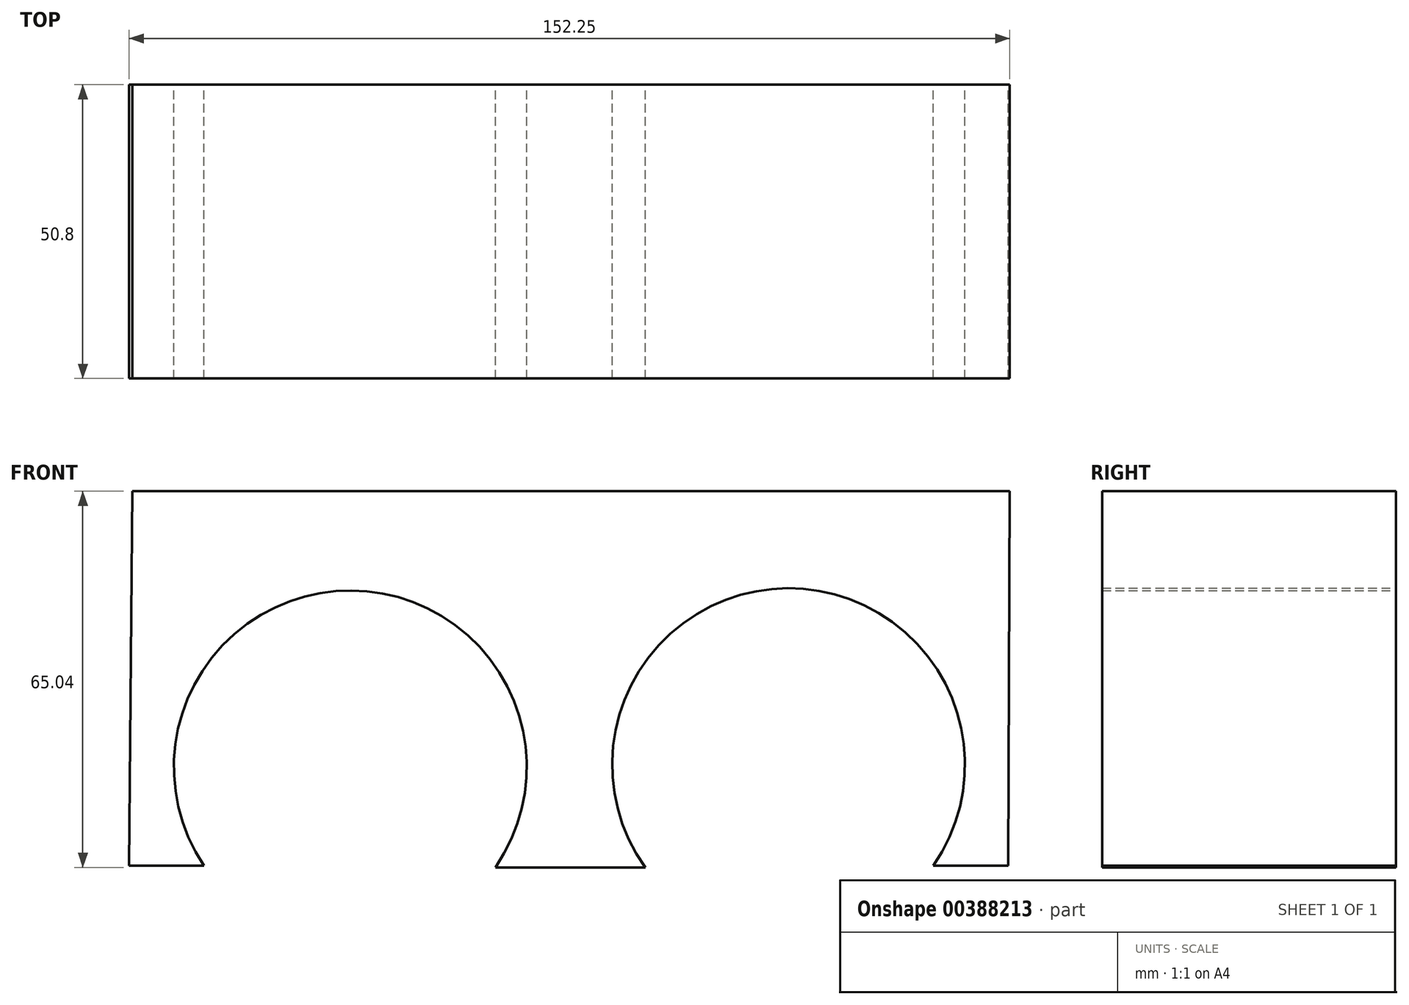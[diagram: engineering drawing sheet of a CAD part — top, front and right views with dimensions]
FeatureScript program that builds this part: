
annotation { "Feature Type Name" : "Feature", "Feature Type Description" : "" }
export const myFeature = defineFeature(function(context is Context, id is Id, definition is map)
    precondition{}
    {
        {
            var Q0;
            Q0=qCreatedBy(makeId("Front.planeOp"),FACE);
            var sketch = newSketch(context, id + "F0", { "sketchPlane" : qUnion([Q0])});
            skLineSegment(sketch, "E0", {"start": v(-75.7, 8.92) * mm, "end": v(75.98, 8.92) * mm});
            skLineSegment(sketch, "E1", {"start": v(-76.27, -55.83) * mm, "end": v(-63.32, -55.83) * mm});
            skLineSegment(sketch, "E2", {"start": v(75.7, -55.83) * mm, "end": v(62.74, -55.83) * mm});
            skLineSegment(sketch, "E3", {"start": v(0, -56.12) * mm, "end": v(12.95, -56.12) * mm});
            skLineSegment(sketch, "E4", {"start": v(12.95, -56.12) * mm, "end": v(0, -56.12) * mm});
            skLineSegment(sketch, "E5", {"start": v(0, -56.12) * mm, "end": v(-12.95, -56.12) * mm});
            skArc(sketch, "E6", {"start": v(-12.95, -56.12) * mm, "mid": v(-37.86, -8.25) * mm, "end": v(-63.32, -55.83) * mm});
            skArc(sketch, "E7", {"start": v(62.74, -55.83) * mm, "mid": v(37.57, -7.85) * mm, "end": v(12.95, -56.12) * mm});
            skLineSegment(sketch, "E8", {"start": v(-76.27, -55.83) * mm, "end": v(-75.7, 8.92) * mm});
            skLineSegment(sketch, "E9", {"start": v(75.7, -55.83) * mm, "end": v(75.98, 8.92) * mm});
            skSolve(sketch);
        }
        {
            var Q0;
            Q0=makeQuery(id+"F0.imprint","IMPRINT",FACE,{"disambiguationData":[TD([[makeQuery(id+"F0.imprint","IMPRINT",EDGE,{"derivedFrom":sQuery(id+"F0.wireOp",EDGE,"E0")}),-1.0]])]});
            extrude(context, id + "F1", {"entities" : qUnion([Q0]), "depth" : 50.8 * mm});
        }
    });
